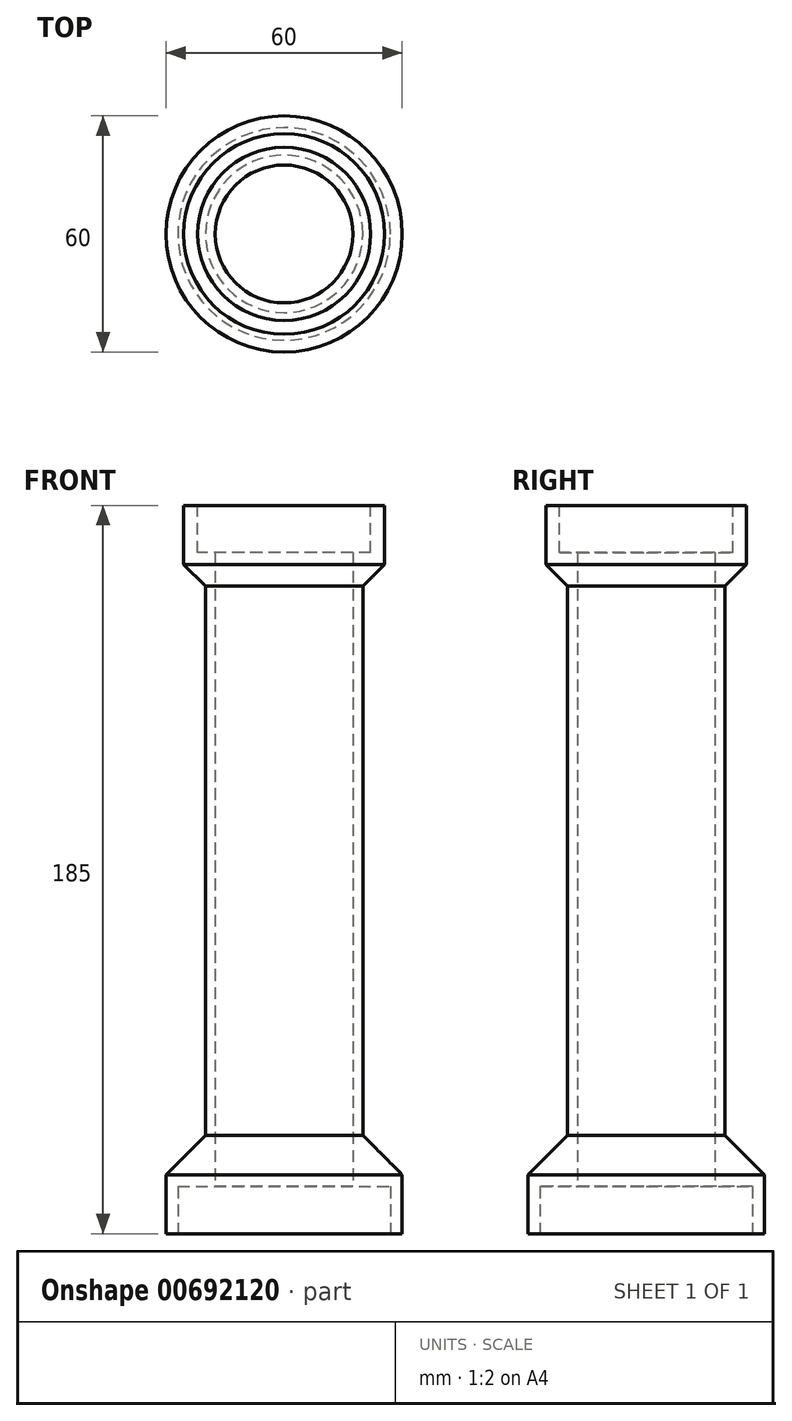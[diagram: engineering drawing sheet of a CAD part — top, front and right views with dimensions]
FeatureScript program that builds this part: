
annotation { "Feature Type Name" : "Feature", "Feature Type Description" : "" }
export const myFeature = defineFeature(function(context is Context, id is Id, definition is map)
    precondition{}
    {
        {
            var Q0;
            Q0=qCreatedBy(makeId("Top.planeOp"),FACE);
            var sketch = newSketch(context, id + "F0", { "sketchPlane" : qUnion([Q0])});
            skCircle(sketch, "E0", {"center": v(0, 0) * mm, "radius": 30 * mm});
            skCircle(sketch, "E1", {"center": v(0, 0) * mm, "radius": 27 * mm});
            skCircle(sketch, "E2", {"center": v(0, 0) * mm, "radius": 22.5 * mm});
            skCircle(sketch, "E3", {"center": v(0, 0) * mm, "radius": 20 * mm});
            skCircle(sketch, "E4", {"center": v(0, 0) * mm, "radius": 17.5 * mm});
            skSolve(sketch);
        }
        {
            var Q0;
            Q0=makeQuery(id+"F0.imprint","IMPRINT",FACE,{"disambiguationData":[TD([[makeQuery(id+"F0.imprint","IMPRINT",EDGE,{"derivedFrom":sQuery(id+"F0.wireOp",EDGE,"E3")}),1.0]])]});
            var Q1;
            Q1=sQuery(id+"F0.wireOp",EDGE,"E3");
            var Q2;
            Q2=sQuery(id+"F0.wireOp",EDGE,"E4");
            extrude(context, id + "F1", {"entities" : qUnion([Q0]), "surfaceOperationType" : NewSurfaceOperationType.ADD, "surfaceEntities" : qUnion([Q1, Q2]), "depth" : 135 * mm, "offsetDistance" : 25 * mm});
        }
        {
            var Q0;
            Q0=qCreatedBy(makeId("Top.planeOp"),FACE);
            var sketch = newSketch(context, id + "F2", { "sketchPlane" : qUnion([Q0])});
            skCircle(sketch, "E5", {"center": v(0, 0) * mm, "radius": 30 * mm});
            skCircle(sketch, "E6", {"center": v(0, 0) * mm, "radius": 27 * mm});
            skCircle(sketch, "E7", {"center": v(0, 0) * mm, "radius": 17.5 * mm});
            skSolve(sketch);
        }
        {
            var Q0;
            Q0=makeQuery(id+"F2.imprint","IMPRINT",FACE,{"disambiguationData":[TD([[makeQuery(id+"F2.imprint","IMPRINT",EDGE,{"derivedFrom":sQuery(id+"F2.wireOp",EDGE,"E5")}),1.0]])]});
            var Q1;
            Q1=makeQuery(id+"F2.imprint","IMPRINT",FACE,{"disambiguationData":[TD([[makeQuery(id+"F2.imprint","IMPRINT",EDGE,{"derivedFrom":sQuery(id+"F2.wireOp",EDGE,"E6")}),1.0]])]});
            extrude(context, id + "F3", {"entities" : qUnion([Q0, Q1]), "operationType" : NewBodyOperationType.ADD, "oppositeDirection" : true, "depth" : 25 * mm, "offsetDistance" : 25 * mm});
        }
        {
            var Q0;
            Q0=makeQuery(id+"F3.opExtrude","CAP_FACE",FACE,{"disambiguationData":[OSD([sQuery(id+"F2.wireOp",EDGE,"E5"),sQuery(id+"F2.wireOp",EDGE,"E7")])],"isStart":false});
            var sketch = newSketch(context, id + "F4", { "sketchPlane" : qUnion([Q0])});
            skCircle(sketch, "E8", {"center": v(0, 0) * mm, "radius": 27 * mm});
            skCircle(sketch, "E9", {"center": v(0, 0) * mm, "radius": 24 * mm});
            skSolve(sketch);
        }
        {
            var Q0;
            Q0=makeQuery(id+"F4.imprint","IMPRINT",FACE,{"disambiguationData":[TD([[makeQuery(id+"F4.imprint","IMPRINT",EDGE,{"derivedFrom":sQuery(id+"F4.wireOp",EDGE,"E9")}),1.0]])]});
            var Q1;
            Q1=makeQuery(id+"F4.imprint","IMPRINT",FACE,{"disambiguationData":[TD([[makeQuery(id+"F4.imprint","IMPRINT",EDGE,{"derivedFrom":sQuery(id+"F4.wireOp",EDGE,"E8")}),1.0]])]});
            var Q2;
            Q2=sQuery(id+"F4.wireOp",EDGE,"E9");
            var Q3;
            Q3=sQuery(id+"F4.wireOp",EDGE,"E8");
            extrude(context, id + "F5", {"entities" : qUnion([Q0, Q1]), "operationType" : NewBodyOperationType.REMOVE, "surfaceOperationType" : NewSurfaceOperationType.ADD, "surfaceEntities" : qUnion([Q2, Q3]), "oppositeDirection" : true, "depth" : 12 * mm, "offsetDistance" : 25 * mm});
        }
        {
            var Q0;
            Q0=makeQuery(id+"F1.opExtrude","CAP_FACE",FACE,{"disambiguationData":[OSD([sQuery(id+"F0.wireOp",EDGE,"E3"),sQuery(id+"F0.wireOp",EDGE,"E4")])],"isStart":false});
            var sketch = newSketch(context, id + "F6", { "sketchPlane" : qUnion([Q0])});
            skCircle(sketch, "E10", {"center": v(0, 0) * mm, "radius": 25.5 * mm});
            skCircle(sketch, "E11", {"center": v(0, 0) * mm, "radius": 22.5 * mm});
            skCircle(sketch, "E12", {"center": v(0, 0) * mm, "radius": 17.5 * mm});
            skSolve(sketch);
        }
        {
            var Q0;
            Q0=makeQuery(id+"F6.imprint","IMPRINT",FACE,{"disambiguationData":[TD([[makeQuery(id+"F6.imprint","IMPRINT",EDGE,{"derivedFrom":sQuery(id+"F6.wireOp",EDGE,"E12")}),-1.0]])]});
            var Q1;
            Q1=makeQuery(id+"F6.imprint","IMPRINT",FACE,{"disambiguationData":[TD([[makeQuery(id+"F6.imprint","IMPRINT",EDGE,{"derivedFrom":sQuery(id+"F6.wireOp",EDGE,"E11")}),1.0]])]});
            var Q2;
            Q2=makeQuery(id+"F6.imprint","IMPRINT",FACE,{"disambiguationData":[TD([[makeQuery(id+"F6.imprint","IMPRINT",EDGE,{"derivedFrom":sQuery(id+"F6.wireOp",EDGE,"E10")}),1.0]])]});
            extrude(context, id + "F7", {"entities" : qUnion([Q0, Q1, Q2]), "operationType" : NewBodyOperationType.ADD, "depth" : 25 * mm, "offsetDistance" : 25 * mm});
        }
        {
            var Q0;
            Q0=makeQuery(id+"F7.opExtrude","CAP_FACE",FACE,{"disambiguationData":[OSD([sQuery(id+"F6.wireOp",EDGE,"E10"),sQuery(id+"F6.wireOp",EDGE,"E12")])],"isStart":false});
            var sketch = newSketch(context, id + "F8", { "sketchPlane" : qUnion([Q0])});
            skCircle(sketch, "E13", {"center": v(0, 0) * mm, "radius": 25.5 * mm});
            skCircle(sketch, "E14", {"center": v(0, 0) * mm, "radius": 22 * mm});
            skCircle(sketch, "E15", {"center": v(0, 10.29) * mm, "radius": 1.26 * mm});
            skSolve(sketch);
        }
        {
            var Q0;
            Q0=makeQuery(id+"F8.imprint","IMPRINT",FACE,{"disambiguationData":[TD([[makeQuery(id+"F8.imprint","IMPRINT",EDGE,{"derivedFrom":sQuery(id+"F8.wireOp",EDGE,"E14")}),1.0]])]});
            extrude(context, id + "F9", {"entities" : qUnion([Q0]), "operationType" : NewBodyOperationType.REMOVE, "oppositeDirection" : true, "depth" : 12 * mm, "offsetDistance" : 25 * mm});
        }
        {
            var Q0;
            Q0=makeQuery(id+"F7.opExtrude","CAP_EDGE",EDGE,{"disambiguationData":[OSD([sQuery(id+"F6.wireOp",EDGE,"E10")])],"isStart":true});
            var Q1;
            Q1=makeQuery(id+"F3.opExtrude","CAP_EDGE",EDGE,{"disambiguationData":[OSD([sQuery(id+"F2.wireOp",EDGE,"E5")])],"isStart":true});
            chamfer(context, id + "F10", {"entities" : qUnion([Q0, Q1]), "width" : 10 * mm, "tangentPropagation" : true});
        }
    });
